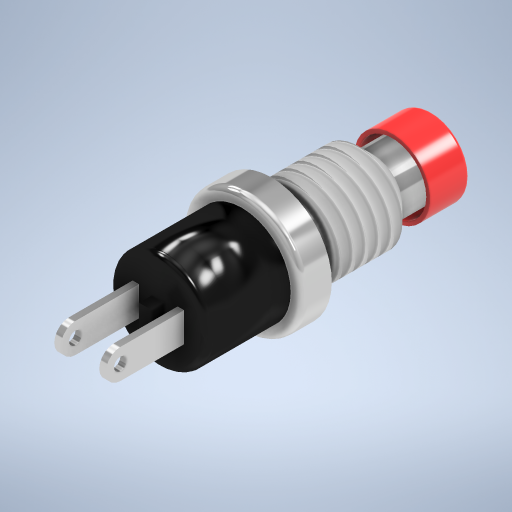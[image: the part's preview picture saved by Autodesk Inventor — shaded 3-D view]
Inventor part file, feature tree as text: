
AUTODESK INVENTOR PART (.ipt)
format: ipt  version: 2023 (Build 270158000, 158)  size: 383,488 bytes
history: native  units: mm
features: sketch x3, extrude x2, revolve x1, thread x1, plane x1, mirror x1
ambient origin geometry x8: Origin, YZ Plane, XZ Plane, XY Plane, X Axis, Y Axis, Z Axis, Center Point
bodies: Solid1 (feature_tree)
feature tree (9):
  revolve  "Revolution1"  [1 undecoded]
  thread  "Thread1"  [1 undecoded]
  plane  "Work Plane1"
  extrude  "Extrusion1"  Depth=4.6mm
  mirror  "Mirror1"
  extrude  "Extrusion2"  Depth=8.8mm
  sketch  "Sketch1"  dims[d0=7.6mm d1=9.4mm d2=5.8mm]
  sketch  "Sketch2"  dims[d3=6.8mm d4=4.6mm]
  sketch  "Sketch3"  dims[d5=2.3mm d6=8.8mm d7=1.4mm d8=5.4mm d9=135.0deg d11=0.5mm d12=21.3mm d13=0.3mm d14=0.3mm d15=5.9mm d16=3.1mm d17=90.0deg d18=0.3mm d19=5.4mm d20=0.0mm d21=1.5mm d22=2.3mm d23=4.95mm d24=1.0mm d25=0.5mm d26=0.0mm d27=1.0mm d28=1.8mm d29=1.0mm d30=0.0mm]
note: 2 required parameter values undecoded (feature->parameter linkage not recoverable at this tier; creation-order binding heuristic only, values carry confidence <= 0.55)